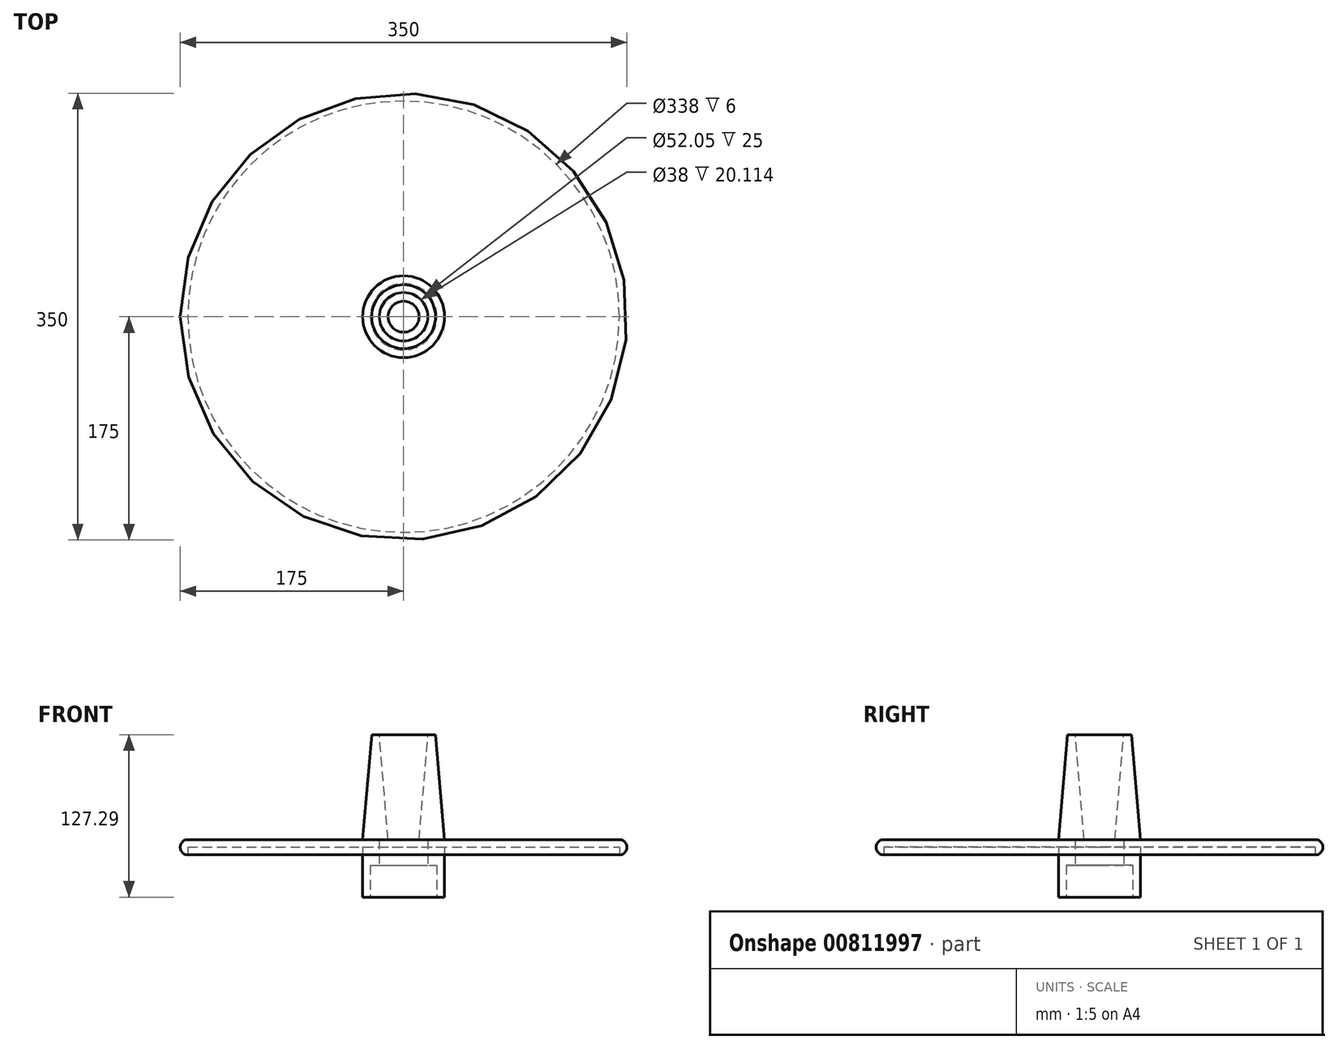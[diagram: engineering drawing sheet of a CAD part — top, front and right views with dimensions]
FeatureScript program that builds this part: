
annotation { "Feature Type Name" : "Feature", "Feature Type Description" : "" }
export const myFeature = defineFeature(function(context is Context, id is Id, definition is map)
    precondition{}
    {
        {
            var Q0;
            Q0=qCreatedBy(makeId("Front.planeOp"),FACE);
            var sketch = newSketch(context, id + "F0", { "sketchPlane" : qUnion([Q0])});
            skLineSegment(sketch, "E0", {"start": v(0, 28.9) * mm, "end": v(0, -53.68) * mm, "construction": true});
            skLineSegment(sketch, "E1", {"start": v(-26.03, -0.3) * mm, "end": v(-26.03, 24.7) * mm});
            skLineSegment(sketch, "E2", {"start": v(-26.03, -0.3) * mm, "end": v(-32.02, -0.3) * mm});
            skPoint(sketch, "E3.end.orphan", {"position": v(-71.46, 14.8) * mm});
            skPoint(sketch, "E4.end.orphan", {"position": v(-71.46, 31.33) * mm});
            skLineSegment(sketch, "E5", {"start": v(-26.03, 24.7) * mm, "end": v(-19, 24.7) * mm});
            skLineSegment(sketch, "E6", {"start": v(-19, 24.7) * mm, "end": v(-19, 44.7) * mm});
            skLineSegment(sketch, "E7", {"start": v(-19, 44.8) * mm, "end": v(-169, 44.8) * mm});
            skPoint(sketch, "E8", {"position": v(-154, -0.3) * mm});
            skPoint(sketch, "E9", {"position": v(-154, 44.8) * mm});
            skLineSegment(sketch, "E10", {"start": v(-32.03, 24.8) * mm, "end": v(-32.03, -0.3) * mm});
            skPoint(sketch, "E11.end.orphan", {"position": v(-179, 44.8) * mm});
            skPoint(sketch, "E11.start.orphan", {"position": v(-281.98, -0.3) * mm});
            skLineSegment(sketch, "E12", {"start": v(-169, 32.8) * mm, "end": v(-169, 44.8) * mm});
            skLineSegment(sketch, "E13", {"start": v(0, 7.2) * mm, "end": v(0, 121.06) * mm, "construction": true});
            skLineSegment(sketch, "E14", {"start": v(-19, 44.7) * mm, "end": v(-19, 44.8) * mm});
            skLineSegment(sketch, "E15", {"start": v(-19, 126.98) * mm, "end": v(-25, 126.98) * mm});
            skLineSegment(sketch, "E16", {"start": v(-25, 126.98) * mm, "end": v(-32.03, 44.7) * mm});
            skArc(sketch, "E17", {"start": v(-169, 44.8) * mm, "mid": v(-175, 38.8) * mm, "end": v(-169, 32.8) * mm});
            skLineSegment(sketch, "E18", {"start": v(-169, 38.8) * mm, "end": v(-32.03, 38.8) * mm});
            skLineSegment(sketch, "E19", {"start": v(-32.03, 38.8) * mm, "end": v(-32.03, 24.8) * mm});
            skLineSegment(sketch, "E20", {"start": v(-32.03, 38.8) * mm, "end": v(-32.03, 44.8) * mm, "construction": true});
            skLineSegment(sketch, "E21", {"start": v(-19, 44.8) * mm, "end": v(-12.14, 44.8) * mm});
            skLineSegment(sketch, "E22", {"start": v(-12.14, 44.8) * mm, "end": v(-19, 126.98) * mm});
            skSolve(sketch);
        }
        {
            var Q0;
            Q0 = qSketchRegion(id + "F0", true);
            var Q1;
            Q1=sQuery(id+"F0.wireOp",EDGE,"E13");
            revolve(context, id + "F1", {"surfaceOperationType" : NewSurfaceOperationType.NEW, "entities" : qUnion([Q0]), "axis" : qUnion([Q1]), "revolveType" : RevolveType.FULL});
        }
        {
            var Q0;
            Q0=makeQuery(id+"F1.opRevolve","SWEPT_FACE",FACE,{"disambiguationData":[OSD([sQuery(id+"F0.wireOp",EDGE,"E18")])]});
            var sketch = newSketch(context, id + "F2", { "sketchPlane" : qUnion([Q0])});
            skCircle(sketch, "E23.0", {"center": v(0, 0) * mm, "radius": 169 * mm, "construction": true});
            skCircle(sketch, "E24.0", {"center": v(0, 0) * mm, "radius": 32.03 * mm, "construction": true});
            skLineSegment(sketch, "E25", {"start": v(0, 169) * mm, "end": v(0, -169) * mm, "construction": true});
            skLineSegment(sketch, "E26", {"start": v(169, 0) * mm, "end": v(-169, 0) * mm, "construction": true});
            skSolve(sketch);
        }
        {
            var Q0;
            Q0=sQuery(id+"F0.wireOp",VERTEX,"E12.start");
            var Q1;
            Q1=sQuery(id+"F0.wireOp",EDGE,"E12");
            cPlane(context, id + "F3", {"entities" : qUnion([Q0, Q1]), "cplaneType" : CPlaneType.LINE_POINT, "offset" : 25 * mm, "width" : 150 * mm, "height" : 150 * mm});
        }
    });
